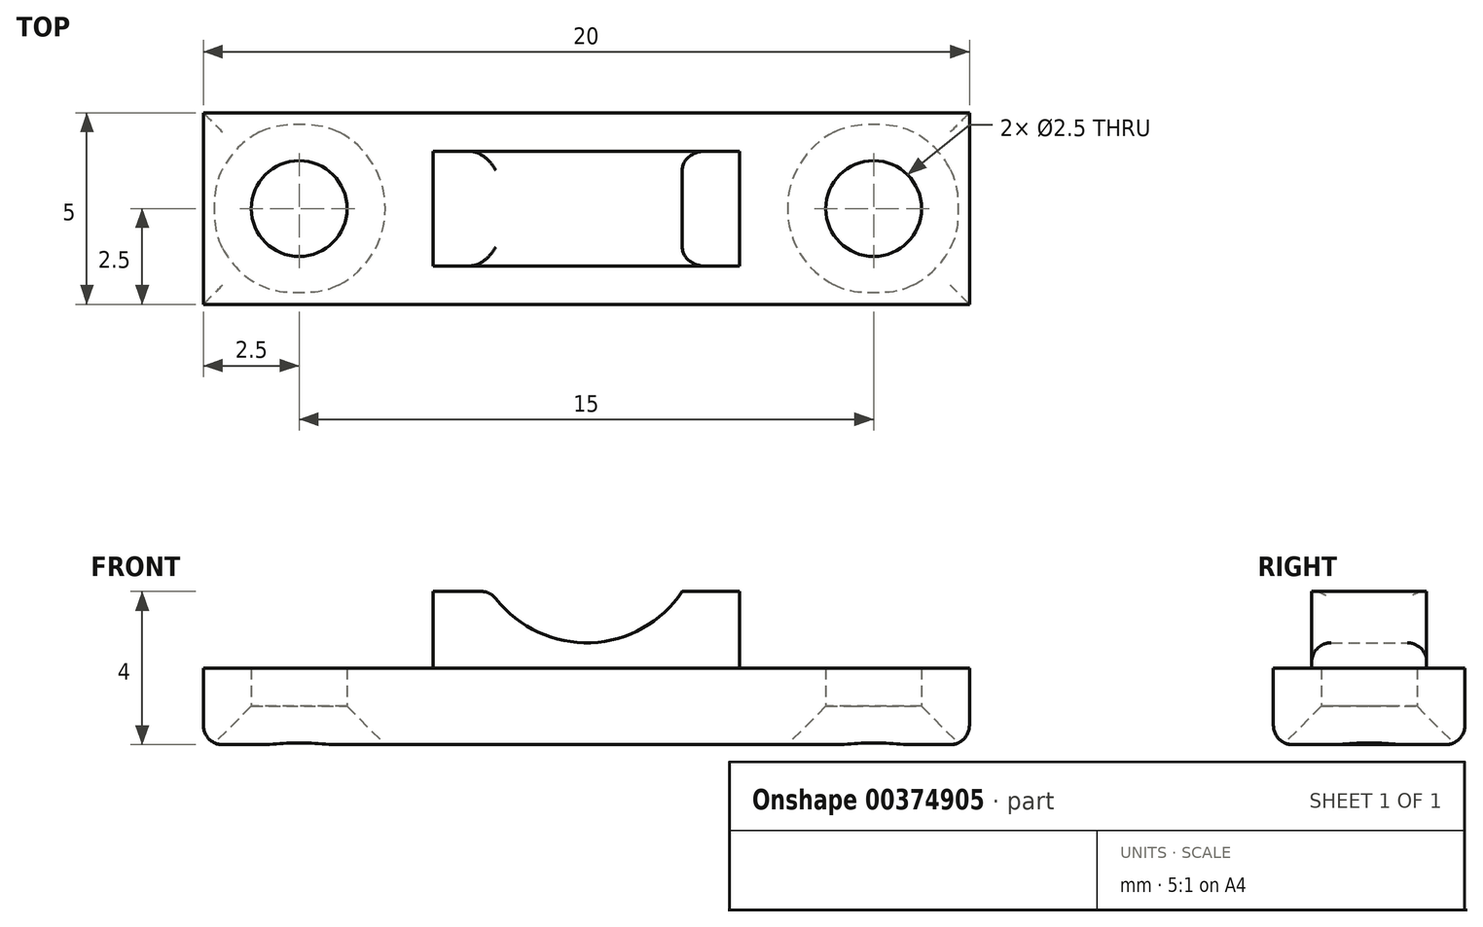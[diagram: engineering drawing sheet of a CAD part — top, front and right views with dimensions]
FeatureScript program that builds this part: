
annotation { "Feature Type Name" : "Feature", "Feature Type Description" : "" }
export const myFeature = defineFeature(function(context is Context, id is Id, definition is map)
    precondition{}
    {
        {
            var Q0;
            Q0=qCreatedBy(makeId("Top.planeOp"),FACE);
            var sketch = newSketch(context, id + "F0", { "sketchPlane" : qUnion([Q0])});
            skLineSegment(sketch, "E0.bottom", {"start": v(-10, 2.5) * mm, "end": v(10, 2.5) * mm});
            skLineSegment(sketch, "E0.top", {"start": v(-10, -2.5) * mm, "end": v(10, -2.5) * mm});
            skLineSegment(sketch, "E0.left", {"start": v(-10, 2.5) * mm, "end": v(-10, -2.5) * mm});
            skLineSegment(sketch, "E0.right", {"start": v(10, 2.5) * mm, "end": v(10, -2.5) * mm});
            skPoint(sketch, "E0.middle", {"position": v(0, 0) * mm});
            skLineSegment(sketch, "E1.bottom", {"start": v(-4, 1.5) * mm, "end": v(4, 1.5) * mm});
            skLineSegment(sketch, "E1.top", {"start": v(-4, -1.5) * mm, "end": v(4, -1.5) * mm});
            skLineSegment(sketch, "E1.left", {"start": v(-4, 1.5) * mm, "end": v(-4, -1.5) * mm});
            skLineSegment(sketch, "E1.right", {"start": v(4, 1.5) * mm, "end": v(4, -1.5) * mm});
            skCircle(sketch, "E2", {"center": v(-7.5, 0) * mm, "radius": 1.25 * mm});
            skCircle(sketch, "E3.MirrorC", {"center": v(7.5, 0) * mm, "radius": 1.25 * mm});
            skSolve(sketch);
        }
        {
            var Q0;
            Q0=makeQuery(id+"F0.imprint","IMPRINT",FACE,{"disambiguationData":[TD([[makeQuery(id+"F0.imprint","IMPRINT",EDGE,{"derivedFrom":sQuery(id+"F0.wireOp",EDGE,"E0.bottom")}),-1.0]])]});
            extrude(context, id + "F1", {"entities" : qUnion([Q0]), "depth" : 2 * mm});
        }
        {
            var Q0;
            Q0=makeQuery(id+"F0.imprint","IMPRINT",FACE,{"disambiguationData":[TD([[makeQuery(id+"F0.imprint","IMPRINT",EDGE,{"derivedFrom":sQuery(id+"F0.wireOp",EDGE,"E1.bottom")}),-1.0]])]});
            extrude(context, id + "F2", {"entities" : qUnion([Q0]), "operationType" : NewBodyOperationType.ADD, "depth" : 4 * mm});
        }
        {
            var Q0;
            Q0=makeQuery(id+"F1.opExtrude","CAP_EDGE",EDGE,{"disambiguationData":[OSD([sQuery(id+"F0.wireOp",EDGE,"E2")])],"isStart":true});
            var Q1;
            Q1=makeQuery(id+"F1.opExtrude","CAP_EDGE",EDGE,{"disambiguationData":[OSD([sQuery(id+"F0.wireOp",EDGE,"E3.MirrorC")])],"isStart":true});
            chamfer(context, id + "F3", {"entities" : qUnion([Q0, Q1]), "width" : 1 * mm, "tangentPropagation" : true});
        }
        {
            var Q0;
            Q0=makeQuery(id+"F1.opExtrude","CAP_EDGE",EDGE,{"disambiguationData":[OSD([sQuery(id+"F0.wireOp",EDGE,"E0.top")])],"isStart":true});
            var Q1;
            Q1=makeQuery(id+"F1.opExtrude","CAP_EDGE",EDGE,{"disambiguationData":[OSD([sQuery(id+"F0.wireOp",EDGE,"E0.bottom")])],"isStart":true});
            var Q2;
            Q2=makeQuery(id+"F1.opExtrude","CAP_EDGE",EDGE,{"disambiguationData":[OSD([sQuery(id+"F0.wireOp",EDGE,"E0.left")])],"isStart":true});
            var Q3;
            Q3=makeQuery(id+"F1.opExtrude","CAP_EDGE",EDGE,{"disambiguationData":[OSD([sQuery(id+"F0.wireOp",EDGE,"E0.right")])],"isStart":true});
            fillet(context, id + "F4", {"entities" : qUnion([Q0, Q1, Q2, Q3]), "radius" : 0.5 * mm, "tangentPropagation" : true, "allowEdgeOverflow" : false});
        }
        {
            var Q0;
            Q0=qCreatedBy(makeId("Front.planeOp"),FACE);
            var sketch = newSketch(context, id + "F5", { "sketchPlane" : qUnion([Q0])});
            skArc(sketch, "E4", {"start": v(-2.5, 4) * mm, "mid": v(0, 2.66) * mm, "end": v(2.5, 4) * mm});
            skLineSegment(sketch, "E5", {"start": v(-2.5, 4) * mm, "end": v(2.5, 4) * mm});
            skSolve(sketch);
        }
        {
            var Q0;
            Q0 = qSketchRegion(id + "F5", true);
            extrude(context, id + "F6", {"entities" : qUnion([Q0]), "operationType" : NewBodyOperationType.REMOVE, "endBound" : BoundingType.SYMMETRIC, "depth" : 25 * mm});
        }
        {
            var Q0;
            Q0=makeQuery(id+"F6.boolean.opBoolean","INTERSECT",EDGE,{"derivedFrom":[makeQuery(id+"F2.opExtrude","SWEPT_FACE",FACE,{"disambiguationData":[OSD([sQuery(id+"F0.wireOp",EDGE,"E1.top")])]}),makeQuery(id+"F6.opExtrude","SWEPT_FACE",FACE,{"disambiguationData":[OSD([sQuery(id+"F5.wireOp",EDGE,"E4")])]})]});
            var Q1;
            Q1=makeQuery(id+"F6.boolean.opBoolean","INTERSECT",EDGE,{"derivedFrom":[makeQuery(id+"F2.opExtrude","SWEPT_FACE",FACE,{"disambiguationData":[OSD([sQuery(id+"F0.wireOp",EDGE,"E1.bottom")])]}),makeQuery(id+"F6.opExtrude","SWEPT_FACE",FACE,{"disambiguationData":[OSD([sQuery(id+"F5.wireOp",EDGE,"E4")])]})]});
            var Q2;
            {var subQ0=sQuery(id+"F5.wireOp",EDGE,"E5");var subQ1=sQuery(id+"F5.wireOp",EDGE,"E4");Q2=makeQuery(id+"F6.boolean.opBoolean","COPY",EDGE,{"derivedFrom":makeQuery(id+"F6.opExtrude","SWEPT_EDGE",EDGE,{"disambiguationData":[OSD([subQ1,subQ0]),TDD([makeQuery(id+"F5.imprint","INTERSECT",VERTEX,{"disambiguationData":[OD(0.0)],"derivedFrom":[subQ1,subQ0]})])]})});}
            var Q3;
            {var subQ0=sQuery(id+"F5.wireOp",EDGE,"E5");var subQ1=sQuery(id+"F5.wireOp",EDGE,"E4");Q3=makeQuery(id+"F6.boolean.opBoolean","COPY",EDGE,{"derivedFrom":makeQuery(id+"F6.opExtrude","SWEPT_EDGE",EDGE,{"disambiguationData":[OSD([subQ1,subQ0]),TDD([makeQuery(id+"F5.imprint","INTERSECT",VERTEX,{"disambiguationData":[OD(1.0)],"derivedFrom":[subQ1,subQ0]})])]})});}
            fillet(context, id + "F7", {"entities" : qUnion([Q0, Q1, Q2, Q3]), "radius" : 0.5 * mm, "tangentPropagation" : true, "allowEdgeOverflow" : false});
        }
    });
